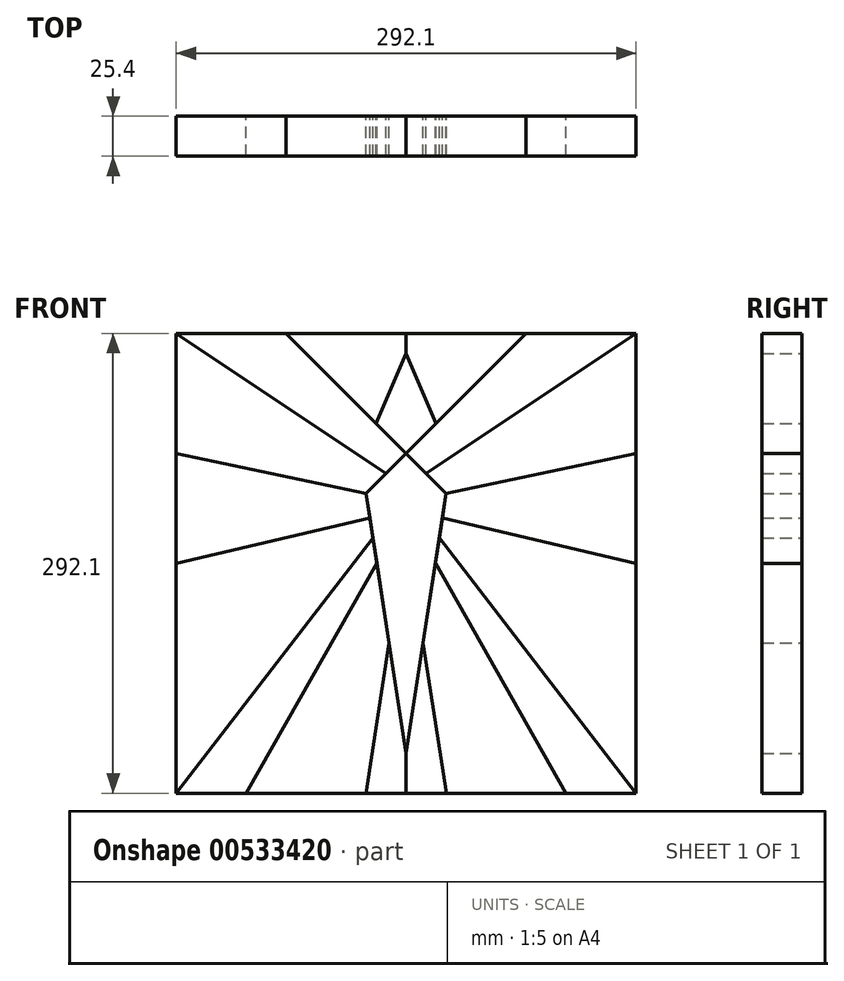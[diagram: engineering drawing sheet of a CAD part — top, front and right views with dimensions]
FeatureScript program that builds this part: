
annotation { "Feature Type Name" : "Feature", "Feature Type Description" : "" }
export const myFeature = defineFeature(function(context is Context, id is Id, definition is map)
    precondition{}
    {
        {
            var Q0;
            Q0=qCreatedBy(makeId("Front.planeOp"),FACE);
            var sketch = newSketch(context, id + "F0", { "sketchPlane" : qUnion([Q0])});
            skLineSegment(sketch, "E0.bottom", {"start": v(-146.05, 146.05) * mm, "end": v(146.05, 146.05) * mm});
            skLineSegment(sketch, "E0.top", {"start": v(-146.05, -146.05) * mm, "end": v(146.05, -146.05) * mm});
            skLineSegment(sketch, "E0.left", {"start": v(-146.05, 146.05) * mm, "end": v(-146.05, -146.05) * mm});
            skLineSegment(sketch, "E0.right", {"start": v(146.05, 146.05) * mm, "end": v(146.05, -146.05) * mm});
            skPoint(sketch, "E0.middle", {"position": v(0, 0) * mm});
            skLineSegment(sketch, "E1", {"start": v(0, 146.05) * mm, "end": v(0, -146.05) * mm, "construction": true});
            skLineSegment(sketch, "E2", {"start": v(-146.05, 0) * mm, "end": v(146.05, 0) * mm, "construction": true});
            skLineSegment(sketch, "E3", {"start": v(0, 133.35) * mm, "end": v(-19.05, 88.9) * mm});
            skLineSegment(sketch, "E4", {"start": v(-19.05, 88.9) * mm, "end": v(0, 69.85) * mm});
            skLineSegment(sketch, "E5", {"start": v(0, 69.85) * mm, "end": v(19.05, 88.9) * mm});
            skLineSegment(sketch, "E6", {"start": v(19.05, 88.9) * mm, "end": v(0, 133.35) * mm});
            skLineSegment(sketch, "E7", {"start": v(0, 69.85) * mm, "end": v(-25.4, 44.45) * mm});
            skLineSegment(sketch, "E8", {"start": v(0, 69.85) * mm, "end": v(25.4, 44.45) * mm});
            skLineSegment(sketch, "E9", {"start": v(25.4, 44.45) * mm, "end": v(0, -120.65) * mm});
            skLineSegment(sketch, "E10", {"start": v(0, -120.65) * mm, "end": v(-25.4, 44.45) * mm});
            skLineSegment(sketch, "E11", {"start": v(-19.05, 88.9) * mm, "end": v(-76.2, 146.05) * mm});
            skLineSegment(sketch, "E12", {"start": v(19.05, 88.9) * mm, "end": v(76.2, 146.05) * mm});
            skLineSegment(sketch, "E13", {"start": v(12.7, 57.15) * mm, "end": v(146.05, 146.05) * mm});
            skLineSegment(sketch, "E14", {"start": v(-12.7, 57.15) * mm, "end": v(-146.05, 146.05) * mm});
            skLineSegment(sketch, "E15", {"start": v(25.4, 44.45) * mm, "end": v(146.05, 69.85) * mm});
            skLineSegment(sketch, "E16", {"start": v(-25.4, 44.45) * mm, "end": v(-146.05, 69.85) * mm});
            skLineSegment(sketch, "E17", {"start": v(22.99, 28.76) * mm, "end": v(146.05, 0) * mm});
            skLineSegment(sketch, "E18", {"start": v(-22.99, 28.76) * mm, "end": v(-146.05, 0) * mm});
            skLineSegment(sketch, "E19", {"start": v(18.61, 0.33) * mm, "end": v(101.6, -146.05) * mm});
            skLineSegment(sketch, "E20", {"start": v(-18.61, 0.33) * mm, "end": v(-101.6, -146.05) * mm});
            skLineSegment(sketch, "E21", {"start": v(-10.8, -50.47) * mm, "end": v(-25.5, -146.05) * mm});
            skLineSegment(sketch, "E22", {"start": v(10.8, -50.47) * mm, "end": v(25.5, -146.05) * mm});
            skLineSegment(sketch, "E23", {"start": v(146.05, -146.05) * mm, "end": v(21.05, 16.2) * mm});
            skLineSegment(sketch, "E24", {"start": v(-146.05, -146.05) * mm, "end": v(-21.05, 16.2) * mm});
            skLineSegment(sketch, "E25", {"start": v(0, 133.35) * mm, "end": v(0, 146.05) * mm});
            skLineSegment(sketch, "E26", {"start": v(0, -120.65) * mm, "end": v(0, -146.05) * mm});
            skSolve(sketch);
        }
        {
            var Q0;
            {var subQ0=sQuery(id+"F0.wireOp",EDGE,"E14");Q0=makeQuery(id+"F0.imprint","IMPRINT",FACE,{"disambiguationData":[TD([[makeQuery(id+"F0.imprint","IMPRINT",EDGE,{"derivedFrom":subQ0}),1.0]])]});}
            var Q1;
            Q1=makeQuery(id+"F0.imprint","IMPRINT",FACE,{"disambiguationData":[TD([[makeQuery(id+"F0.imprint","IMPRINT",EDGE,{"derivedFrom":sQuery(id+"F0.wireOp",EDGE,"E3")}),-1.0]])]});
            var Q2;
            {var subQ2=sQuery(id+"F0.wireOp",EDGE,"E5");Q2=makeQuery(id+"F0.imprint","IMPRINT",FACE,{"disambiguationData":[TD([[makeQuery(id+"F0.imprint","IMPRINT",EDGE,{"derivedFrom":subQ2}),-1.0]])]});}
            var Q3;
            {var subQ0=sQuery(id+"F0.wireOp",EDGE,"E15");Q3=makeQuery(id+"F0.imprint","IMPRINT",FACE,{"disambiguationData":[TD([[makeQuery(id+"F0.imprint","IMPRINT",EDGE,{"derivedFrom":subQ0}),-1.0]])]});}
            var Q4;
            {var subQ2=sQuery(id+"F0.wireOp",EDGE,"E19");Q4=makeQuery(id+"F0.imprint","IMPRINT",FACE,{"disambiguationData":[TD([[makeQuery(id+"F0.imprint","IMPRINT",EDGE,{"derivedFrom":subQ2}),1.0]])]});}
            var Q5;
            {var subQ0=sQuery(id+"F0.wireOp",EDGE,"E22");Q5=makeQuery(id+"F0.imprint","IMPRINT",FACE,{"disambiguationData":[TD([[makeQuery(id+"F0.imprint","IMPRINT",EDGE,{"derivedFrom":subQ0}),-1.0]])]});}
            var Q6;
            {var subQ0=sQuery(id+"F0.wireOp",EDGE,"E20");Q6=makeQuery(id+"F0.imprint","IMPRINT",FACE,{"disambiguationData":[TD([[makeQuery(id+"F0.imprint","IMPRINT",EDGE,{"derivedFrom":subQ0}),1.0]])]});}
            var Q7;
            {var subQ2=sQuery(id+"F0.wireOp",EDGE,"E18");Q7=makeQuery(id+"F0.imprint","IMPRINT",FACE,{"disambiguationData":[TD([[makeQuery(id+"F0.imprint","IMPRINT",EDGE,{"derivedFrom":subQ2}),1.0]])]});}
            extrude(context, id + "F1", {"entities" : qUnion([Q0, Q1, Q2, Q3, Q4, Q5, Q6, Q7]), "depth" : 25.4 * mm, "offsetDistance" : 25.4 * mm});
        }
        {
            var Q0;
            {var subQ0=sQuery(id+"F0.wireOp",EDGE,"E16");Q0=makeQuery(id+"F0.imprint","IMPRINT",FACE,{"disambiguationData":[TD([[makeQuery(id+"F0.imprint","IMPRINT",EDGE,{"derivedFrom":subQ0}),1.0]])]});}
            var Q1;
            {var subQ1=sQuery(id+"F0.wireOp",EDGE,"E4");Q1=makeQuery(id+"F0.imprint","IMPRINT",FACE,{"disambiguationData":[TD([[makeQuery(id+"F0.imprint","IMPRINT",EDGE,{"derivedFrom":subQ1}),-1.0]])]});}
            var Q2;
            Q2=makeQuery(id+"F0.imprint","IMPRINT",FACE,{"disambiguationData":[TD([[makeQuery(id+"F0.imprint","IMPRINT",EDGE,{"derivedFrom":sQuery(id+"F0.wireOp",EDGE,"E6")}),-1.0]])]});
            var Q3;
            {var subQ0=sQuery(id+"F0.wireOp",EDGE,"E13");Q3=makeQuery(id+"F0.imprint","IMPRINT",FACE,{"disambiguationData":[TD([[makeQuery(id+"F0.imprint","IMPRINT",EDGE,{"derivedFrom":subQ0}),-1.0]])]});}
            var Q4;
            {var subQ2=sQuery(id+"F0.wireOp",EDGE,"E17");Q4=makeQuery(id+"F0.imprint","IMPRINT",FACE,{"disambiguationData":[TD([[makeQuery(id+"F0.imprint","IMPRINT",EDGE,{"derivedFrom":subQ2}),-1.0]])]});}
            var Q5;
            {var subQ0=sQuery(id+"F0.wireOp",EDGE,"E19");Q5=makeQuery(id+"F0.imprint","IMPRINT",FACE,{"disambiguationData":[TD([[makeQuery(id+"F0.imprint","IMPRINT",EDGE,{"derivedFrom":subQ0}),-1.0]])]});}
            var Q6;
            {var subQ0=sQuery(id+"F0.wireOp",EDGE,"E21");Q6=makeQuery(id+"F0.imprint","IMPRINT",FACE,{"disambiguationData":[TD([[makeQuery(id+"F0.imprint","IMPRINT",EDGE,{"derivedFrom":subQ0}),1.0]])]});}
            var Q7;
            {var subQ2=sQuery(id+"F0.wireOp",EDGE,"E20");Q7=makeQuery(id+"F0.imprint","IMPRINT",FACE,{"disambiguationData":[TD([[makeQuery(id+"F0.imprint","IMPRINT",EDGE,{"derivedFrom":subQ2}),-1.0]])]});}
            extrude(context, id + "F2", {"entities" : qUnion([Q0, Q1, Q2, Q3, Q4, Q5, Q6, Q7]), "depth" : 25.4 * mm, "offsetDistance" : 25.4 * mm});
        }
        {
            var Q0;
            Q0=makeQuery(id+"F0.imprint","IMPRINT",FACE,{"disambiguationData":[TD([[makeQuery(id+"F0.imprint","IMPRINT",EDGE,{"derivedFrom":sQuery(id+"F0.wireOp",EDGE,"E3")}),1.0]])]});
            var Q1;
            {var subQ1=sQuery(id+"F0.wireOp",EDGE,"E9");var subQ7=makeQuery(id+"F0.imprint","INTERSECT",VERTEX,{"derivedFrom":[subQ1,sQuery(id+"F0.wireOp",EDGE,"E17")]});Q1=makeQuery(id+"F0.imprint","IMPRINT",FACE,{"disambiguationData":[TD([[makeQuery(id+"F0.imprint","IMPRINT",EDGE,{"disambiguationData":[TD([[subQ7,-1.0]])],"derivedFrom":subQ1}),-1.0]])]});}
            extrude(context, id + "F3", {"entities" : qUnion([Q0, Q1]), "depth" : 25.4 * mm, "offsetDistance" : 25.4 * mm});
        }
    });
